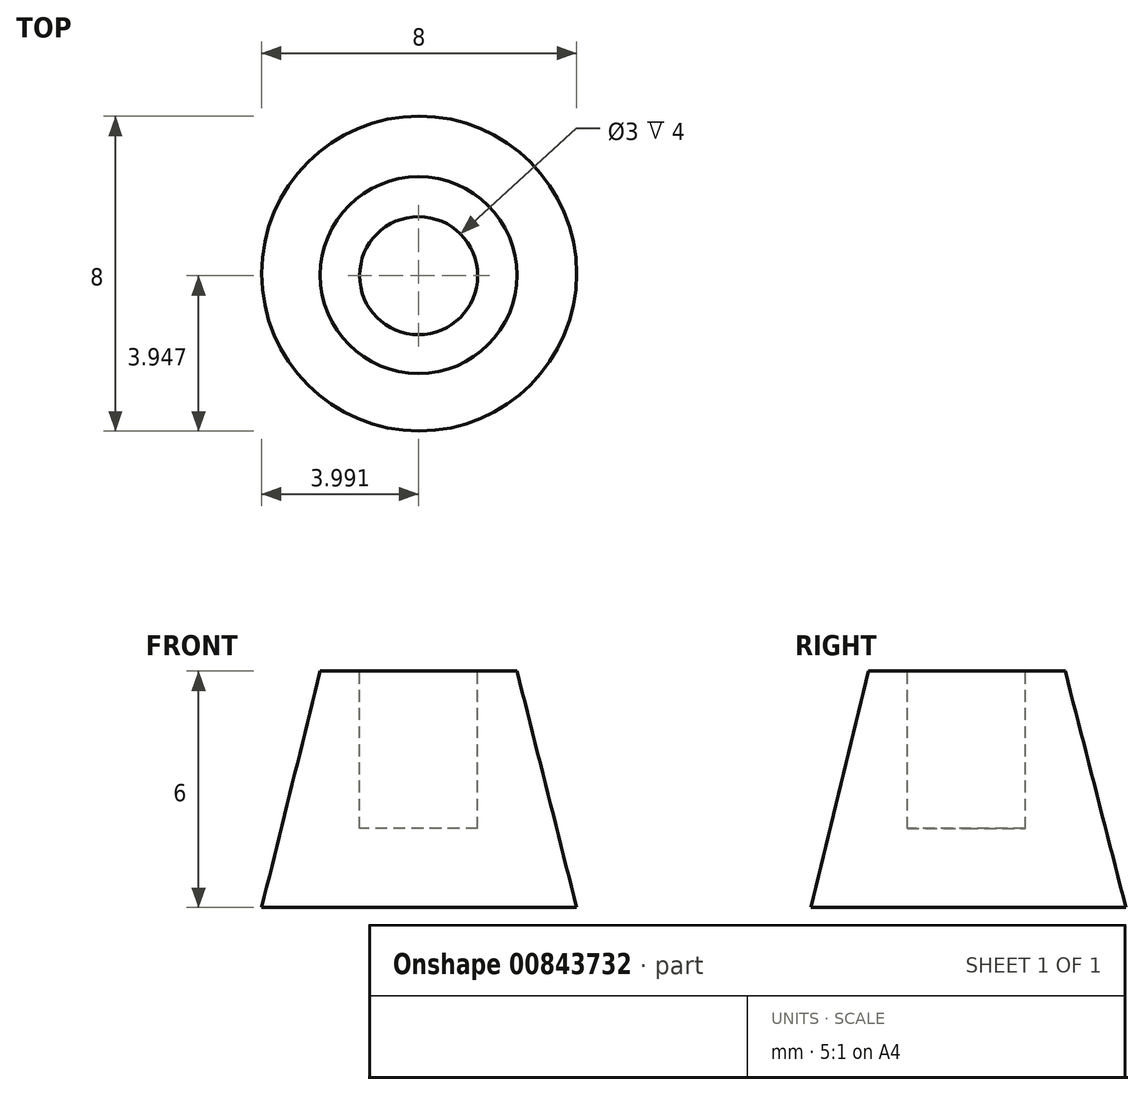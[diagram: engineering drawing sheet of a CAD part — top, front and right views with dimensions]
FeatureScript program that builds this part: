
annotation { "Feature Type Name" : "Feature", "Feature Type Description" : "" }
export const myFeature = defineFeature(function(context is Context, id is Id, definition is map)
    precondition{}
    {
        {
            var Q0;
            Q0=qCreatedBy(makeId("Top.planeOp"),FACE);
            var sketch = newSketch(context, id + "F0", { "sketchPlane" : qUnion([Q0])});
            skCircle(sketch, "E0", {"center": v(0, 0) * mm, "radius": 1.5 * mm});
            skCircle(sketch, "E1", {"center": v(0, 0) * mm, "radius": 4 * mm});
            skCircle(sketch, "E2", {"center": v(0, 0) * mm, "radius": 2.5 * mm});
            skSolve(sketch);
        }
        {
            var Q0;
            Q0=makeQuery(id+"F0.imprint","IMPRINT",FACE,{"disambiguationData":[TD([[makeQuery(id+"F0.imprint","IMPRINT",EDGE,{"derivedFrom":sQuery(id+"F0.wireOp",EDGE,"E0")}),-1.0]])]});
            extrude(context, id + "F1", {"entities" : qUnion([Q0]), "depth" : 6 * mm, "offsetDistance" : 25 * mm});
        }
        {
            var Q0;
            Q0=makeQuery(id+"F1.opExtrude","CAP_FACE",FACE,{"disambiguationData":[OSD([sQuery(id+"F0.wireOp",EDGE,"E0"),sQuery(id+"F0.wireOp",EDGE,"E2")])],"isStart":false});
            var sketch = newSketch(context, id + "F2", { "sketchPlane" : qUnion([Q0])});
            skCircle(sketch, "E3", {"center": v(0, 0) * mm, "radius": 2.5 * mm});
            skSolve(sketch);
        }
        {
            var Q0;
            Q0=makeQuery(id+"F0.imprint","IMPRINT",FACE,{"disambiguationData":[TD([[makeQuery(id+"F0.imprint","IMPRINT",EDGE,{"derivedFrom":sQuery(id+"F0.wireOp",EDGE,"E1")}),1.0]])]});
            var sketch = newSketch(context, id + "F3", { "sketchPlane" : qUnion([Q0])});
            skCircle(sketch, "E4", {"center": v(0.01, 0.04) * mm, "radius": 4 * mm});
            skSolve(sketch);
        }
        {
            var Q1;
            Q1 = qSketchRegion(id + "F2", true);
            var Q2;
            Q2 = qSketchRegion(id + "F3", true);
            loft(context, id + "F4", {"operationType" : NewBodyOperationType.ADD, "sheetProfilesArray" : [{ "sheetProfileEntities" : qUnion([Q1]) }, { "sheetProfileEntities" : qUnion([Q2]) }]});
        }
        {
            var Q0;
            {var subQ0=sQuery(id+"F0.wireOp",EDGE,"E0");Q0=makeQuery(id+"F4.boolean.opBoolean","MERGE",FACE,{"derivedFrom":[makeQuery(id+"F1.opExtrude","CAP_FACE",FACE,{"disambiguationData":[OSD([subQ0,sQuery(id+"F0.wireOp",EDGE,"E2")])],"isStart":false}),makeQuery(id+"F4.opLoft","CAP_FACE",FACE,{"disambiguationData":[OSD([makeQuery(id+"F2.imprint","IMPRINT",FACE,{"disambiguationData":[TD([[makeQuery(id+"F2.imprint","IMPRINT",EDGE,{"derivedFrom":makeQuery(id+"F1.opExtrude","CAP_EDGE",EDGE,{"disambiguationData":[OSD([subQ0])],"isStart":false})}),1.0]])]})])],"isStart":true})]});}
            var sketch = newSketch(context, id + "F5", { "sketchPlane" : qUnion([Q0])});
            skCircle(sketch, "E5", {"center": v(0, -0.01) * mm, "radius": 1.5 * mm});
            skSolve(sketch);
        }
        {
            var Q0;
            Q0=makeQuery(id+"F5.imprint","IMPRINT",FACE,{"disambiguationData":[TD([[makeQuery(id+"F5.imprint","IMPRINT",EDGE,{"derivedFrom":sQuery(id+"F5.wireOp",EDGE,"E5")}),1.0]])]});
            extrude(context, id + "F6", {"entities" : qUnion([Q0]), "operationType" : NewBodyOperationType.REMOVE, "oppositeDirection" : true, "depth" : 4 * mm, "offsetDistance" : 25 * mm});
        }
    });
